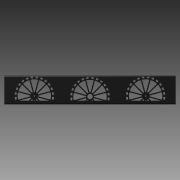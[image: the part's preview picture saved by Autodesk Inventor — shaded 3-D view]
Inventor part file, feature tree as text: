
AUTODESK INVENTOR PART (.ipt)
format: ipt  version: 2014 SP1 (Build 180222100, 222)  size: 999,424 bytes
history: native  units: in
note: dims shown in document units (in); Inventor stores cm internally (conversion verified against a paired STEP export)
features: other x4, sketch x4, extrude x2, sheet_metal_op x2, hole x1, imported_body x1
ambient origin geometry x8: Origin, YZ Plane, XZ Plane, XY Plane, X Axis, Y Axis, Z Axis, Center Point
bodies: Body1 (feature_tree)
feature tree (14):
  other  "PartBody"
  other  "Part21"
  extrude  "Extrusion1"  Depth=0.09in
  extrude  "Extrusion2"  Depth=0.09in
  sheet_metal_op  "Flange1"
  hole  "Hole1"  [1 undecoded]
  imported_body  "Base1"
  sketch  "Sketch1"  dims[d0=0.09in d1=0.045in]
  other  "Plate1"
  sheet_metal_op  "Bend1"
  sketch  "Sketch2"  dims[d2=0.18in d3=0.09in]
  sketch  "Sketch3"  dims[d4=1.18in d5=90.0deg d6=0.09in d7=0.36in]
  sketch  "Sketch4"  dims[d8=0.09in d9=0.09in d19=0.266in d20=0.75in d21=0.375in d22=0.25in d23=0.5635in d24=0.09in d25=0.8108in d26=0.375in d27=1.0in d28=0.0in d29=0.375in d30=1.0in d31=0.0in d32=0.5in d33=0.5in d34=14.1732in d36=1.0in d37=0.3937in d39=1.0in]
  other  "Definition1"
note: 1 required parameter value undecoded (feature->parameter linkage not recoverable at this tier; creation-order binding heuristic only, values carry confidence <= 0.55)
